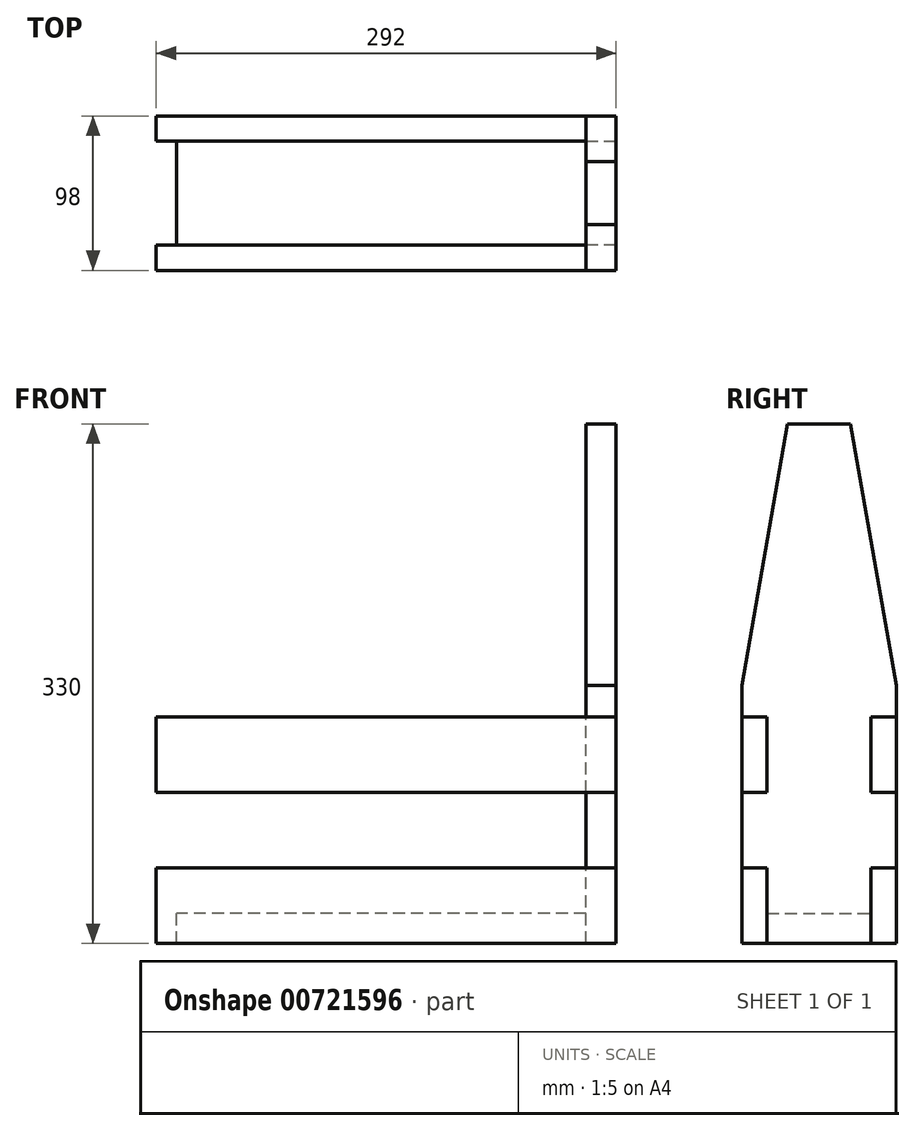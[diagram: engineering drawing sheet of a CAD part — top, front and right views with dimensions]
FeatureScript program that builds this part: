
annotation { "Feature Type Name" : "Feature", "Feature Type Description" : "" }
export const myFeature = defineFeature(function(context is Context, id is Id, definition is map)
    precondition{}
    {
        {
            var Q0;
            Q0=qCreatedBy(makeId("Right.planeOp"),FACE);
            var sketch = newSketch(context, id + "F0", { "sketchPlane" : qUnion([Q0])});
            skLineSegment(sketch, "E0.bottom", {"start": v(0, 0) * mm, "end": v(66, 0) * mm});
            skLineSegment(sketch, "E0.top", {"start": v(0, 19) * mm, "end": v(66, 19) * mm});
            skLineSegment(sketch, "E0.left", {"start": v(0, 0) * mm, "end": v(0, 19) * mm});
            skLineSegment(sketch, "E0.right", {"start": v(66, 0) * mm, "end": v(66, 19) * mm});
            skSolve(sketch);
        }
        {
            var Q0;
            Q0 = qSketchRegion(id + "F0", true);
            extrude(context, id + "F1", {"entities" : qUnion([Q0]), "depth" : 260 * mm, "offsetDistance" : 25 * mm});
        }
        {
            var Q0;
            Q0=makeQuery(id+"F1.opExtrude","CAP_FACE",FACE,{"disambiguationData":[OSD([sQuery(id+"F0.wireOp",EDGE,"E0.bottom"),sQuery(id+"F0.wireOp",EDGE,"E0.top"),sQuery(id+"F0.wireOp",EDGE,"E0.left"),sQuery(id+"F0.wireOp",EDGE,"E0.right")])],"isStart":false});
            var sketch = newSketch(context, id + "F2", { "sketchPlane" : qUnion([Q0])});
            skLineSegment(sketch, "E1.0", {"start": v(0, 0) * mm, "end": v(66, 0) * mm});
            skLineSegment(sketch, "E2", {"start": v(0, 0) * mm, "end": v(0, 48) * mm});
            skLineSegment(sketch, "E3", {"start": v(0, 48) * mm, "end": v(-16, 48) * mm});
            skLineSegment(sketch, "E4", {"start": v(-16, 48) * mm, "end": v(-16, 96) * mm});
            skLineSegment(sketch, "E5", {"start": v(-16, 96) * mm, "end": v(0, 96) * mm});
            skLineSegment(sketch, "E6", {"start": v(0, 96) * mm, "end": v(0, 144) * mm});
            skLineSegment(sketch, "E7", {"start": v(0, 144) * mm, "end": v(-16, 144) * mm});
            skLineSegment(sketch, "E8", {"start": v(-16, 144) * mm, "end": v(-16, 164) * mm});
            skLineSegment(sketch, "E9", {"start": v(-16, 164) * mm, "end": v(13, 330) * mm});
            skLineSegment(sketch, "E10", {"start": v(33, 0) * mm, "end": v(33, 128.36) * mm, "construction": true});
            skLineSegment(sketch, "E11", {"start": v(13, 330) * mm, "end": v(33, 330) * mm});
            skLineSegment(sketch, "E12.MirrorCS", {"start": v(66, 0) * mm, "end": v(66, 48) * mm});
            skLineSegment(sketch, "E13.MirrorCS", {"start": v(66, 48) * mm, "end": v(82, 48) * mm});
            skLineSegment(sketch, "E14.MirrorCS", {"start": v(82, 48) * mm, "end": v(82, 96) * mm});
            skLineSegment(sketch, "E15.MirrorCS", {"start": v(82, 96) * mm, "end": v(66, 96) * mm});
            skLineSegment(sketch, "E16.MirrorCS", {"start": v(66, 96) * mm, "end": v(66, 144) * mm});
            skLineSegment(sketch, "E17.MirrorCS", {"start": v(66, 144) * mm, "end": v(82, 144) * mm});
            skLineSegment(sketch, "E18.MirrorCS", {"start": v(82, 144) * mm, "end": v(82, 164) * mm});
            skLineSegment(sketch, "E19.MirrorCS", {"start": v(82, 164) * mm, "end": v(53, 330) * mm});
            skLineSegment(sketch, "E20.MirrorCS", {"start": v(53, 330) * mm, "end": v(33, 330) * mm});
            skSolve(sketch);
        }
        {
            var Q0;
            {var subQ4=sQuery(id+"F2.wireOp",EDGE,"E3");Q0=makeQuery(id+"F2.imprint","IMPRINT",FACE,{"disambiguationData":[TD([[makeQuery(id+"F2.imprint","IMPRINT",EDGE,{"derivedFrom":subQ4}),-1.0]])]});}
            var Q1;
            {var subQ0=sQuery(id+"F2.wireOp",EDGE,"E1.0");Q1=makeQuery(id+"F2.imprint","IMPRINT",FACE,{"disambiguationData":[TD([[makeQuery(id+"F2.imprint","IMPRINT",EDGE,{"derivedFrom":subQ0}),1.0]])]});}
            extrude(context, id + "F3", {"entities" : qUnion([Q0, Q1]), "depth" : 19 * mm, "offsetDistance" : 25 * mm});
        }
        {
            var Q0;
            Q0=makeQuery(id+"F3.opExtrude","CAP_FACE",FACE,{"disambiguationData":[OSD([sQuery(id+"F2.wireOp",EDGE,"E1.0"),sQuery(id+"F2.wireOp",EDGE,"E2"),sQuery(id+"F2.wireOp",EDGE,"E3"),sQuery(id+"F2.wireOp",EDGE,"E4"),sQuery(id+"F2.wireOp",EDGE,"E5"),sQuery(id+"F2.wireOp",EDGE,"E6"),sQuery(id+"F2.wireOp",EDGE,"E7"),sQuery(id+"F2.wireOp",EDGE,"E8"),sQuery(id+"F2.wireOp",EDGE,"E9"),sQuery(id+"F2.wireOp",EDGE,"E11"),sQuery(id+"F2.wireOp",EDGE,"E12.MirrorCS"),sQuery(id+"F2.wireOp",EDGE,"E13.MirrorCS"),sQuery(id+"F2.wireOp",EDGE,"E14.MirrorCS"),sQuery(id+"F2.wireOp",EDGE,"E15.MirrorCS"),sQuery(id+"F2.wireOp",EDGE,"E16.MirrorCS"),sQuery(id+"F2.wireOp",EDGE,"E17.MirrorCS"),sQuery(id+"F2.wireOp",EDGE,"E18.MirrorCS"),sQuery(id+"F2.wireOp",EDGE,"E19.MirrorCS"),sQuery(id+"F2.wireOp",EDGE,"E20.MirrorCS")])],"isStart":false});
            var sketch = newSketch(context, id + "F4", { "sketchPlane" : qUnion([Q0])});
            skLineSegment(sketch, "E21.bottom", {"start": v(0, 48) * mm, "end": v(-16, 48) * mm});
            skLineSegment(sketch, "E21.top", {"start": v(0, 0) * mm, "end": v(-16, 0) * mm});
            skLineSegment(sketch, "E21.left", {"start": v(0, 48) * mm, "end": v(0, 0) * mm});
            skLineSegment(sketch, "E21.right", {"start": v(-16, 48) * mm, "end": v(-16, 0) * mm});
            skLineSegment(sketch, "E22.bottom", {"start": v(-16, 144) * mm, "end": v(0, 144) * mm});
            skLineSegment(sketch, "E22.top", {"start": v(-16, 96) * mm, "end": v(0, 96) * mm});
            skLineSegment(sketch, "E22.left", {"start": v(-16, 144) * mm, "end": v(-16, 96) * mm});
            skLineSegment(sketch, "E22.right", {"start": v(0, 144) * mm, "end": v(0, 96) * mm});
            skLineSegment(sketch, "E23.bottom", {"start": v(82, 144) * mm, "end": v(66, 144) * mm});
            skLineSegment(sketch, "E23.top", {"start": v(82, 96) * mm, "end": v(66, 96) * mm});
            skLineSegment(sketch, "E23.left", {"start": v(82, 144) * mm, "end": v(82, 96) * mm});
            skLineSegment(sketch, "E23.right", {"start": v(66, 144) * mm, "end": v(66, 96) * mm});
            skLineSegment(sketch, "E24.bottom", {"start": v(66, 0) * mm, "end": v(82, 0) * mm});
            skLineSegment(sketch, "E24.top", {"start": v(66, 48) * mm, "end": v(82, 48) * mm});
            skLineSegment(sketch, "E24.left", {"start": v(66, 0) * mm, "end": v(66, 48) * mm});
            skLineSegment(sketch, "E24.right", {"start": v(82, 0) * mm, "end": v(82, 48) * mm});
            skSolve(sketch);
        }
        {
            var Q0;
            Q0 = qSketchRegion(id + "F4", true);
            extrude(context, id + "F5", {"entities" : qUnion([Q0]), "oppositeDirection" : true, "depth" : 292 * mm, "offsetDistance" : 25 * mm});
        }
    });
